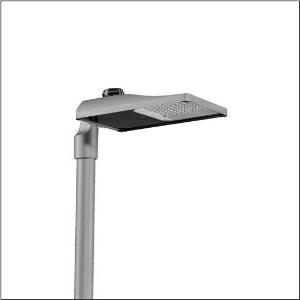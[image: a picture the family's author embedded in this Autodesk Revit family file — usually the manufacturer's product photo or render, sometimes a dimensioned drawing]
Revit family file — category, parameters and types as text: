
# Revit family: streetlight_sl_31_midi___st1_5a_5xh7p7bn08ma_0bef
name_source: partatom
category: Lighting Fixtures
units: mm (PartAtom-declared; Revit-internal decimal feet)

## family parameters
Cut with Voids When Loaded = No
Host = Face
Light Source = No
Part Type = Normal
Room Calculation Point = No
Round Connector Dimension = Use Diameter
Shared = No

## types (1)
- --- (1 x LED, 15480 lm, 145.3 W, 2200K)
    Apparent Load = 145 VA
    CIE Flux Codes = 22 53 95 100 100
    Color Rendering = 70
    Color Temperature = 2200K
    Default Elevation = 1800 mm
    Description = Streetlight SL 31 midi NEMA (7pin) mast luminaire for post-top, side-entry; light control with lens of PMMA; light distribution: ST1.5a, direct asymmetric distribution, for standard-compliant lighting for roads and squares; LED: luminous flux: 15.480lm, light colour: 722, colour temperature: 2200K; luminous efficacy: 106,5lm/W; control: pre-setting: linear dimming characteristic, flexible luminous flux parameterisation, time-dependent luminous flux control, constant luminous flux control, intelligent temperature release in ECG and LED module, overheat protection; luminaire housing, of diecast aluminium, SITECO metallic grey (DB 702S), corrosivity category C5 high according to DIN EN ISO 12944; cover of toughened safety glass, transparent, opened without tools; mast flange of diecast aluminium, SITECO metallic grey (DB 702S), spigot size: 76/60mm, mast flange included unmounted; cable length: 12,5m, connection cable pre-assembled; mains connection: 220..240V, AC, 50/60Hz; power consumption (at start of service life): 145,3W / (at end of service life): 161,8W / (with reduced operation 50%): 61,1W; protection rating (complete): IP66; insulation class (complete): insulation class I (protective earthing); impact resistance: IK10; certification: CE, ENEC, ENEC+, VDE, UKCA; permissible operating ambient temperature for outdoor applications: -40..+50°C; packaging unit: 1 piece

Light Distribution: ST1.5a
    Height = 79 mm
    Lamp = 1 x LED
    Lamp Light Flux = 15480 lm
    Lamp Power = 145.3 W
    Lamp count = 1
    Length = 577 mm
    Luminous efficacy = 107 lm/W
    Manufacturer = Siteco
    ModVariant = No
    Model = 5XH7P7BN08MA
    Number of Poles = 1
    OnlyDefault = Yes
    Power Factor = 1
    Product Name = Streetlight SL 31 midi | ST1.5a
    Product group = mast luminaire | pylon top
    ProductGroupID = 6100
    Protection Class = Protection class I
    Protection Degree = IP 66
    RLX_Detail_Level = 1
    RLX_Emergency_Light_Flux = 0 lm
    RLX_Emergency_Type = 0
    RLX_Emergency_Type_DB = No
    RlxData = <blob elided: 29797 chars, md5=238d2b15>
    Socket = socket
    Standby Power = 0 W
    System Light Flux = 15480 lm
    System Power = 145 W
    Type Comments = factory setting: luminous flux: 100 % | dim-lin: 254 | 747 mA
    Type Image = l_1300282.jpg
    URL = http://relux.com
    VarID = @adj_009775
    Voltage = 0 V
    Weight = 0.00 kg
    Width = 362 mm

## geometry (parser evidence)
native form markers: Blend x4, Sweep x8
no freeform markers — native parametric forms only
